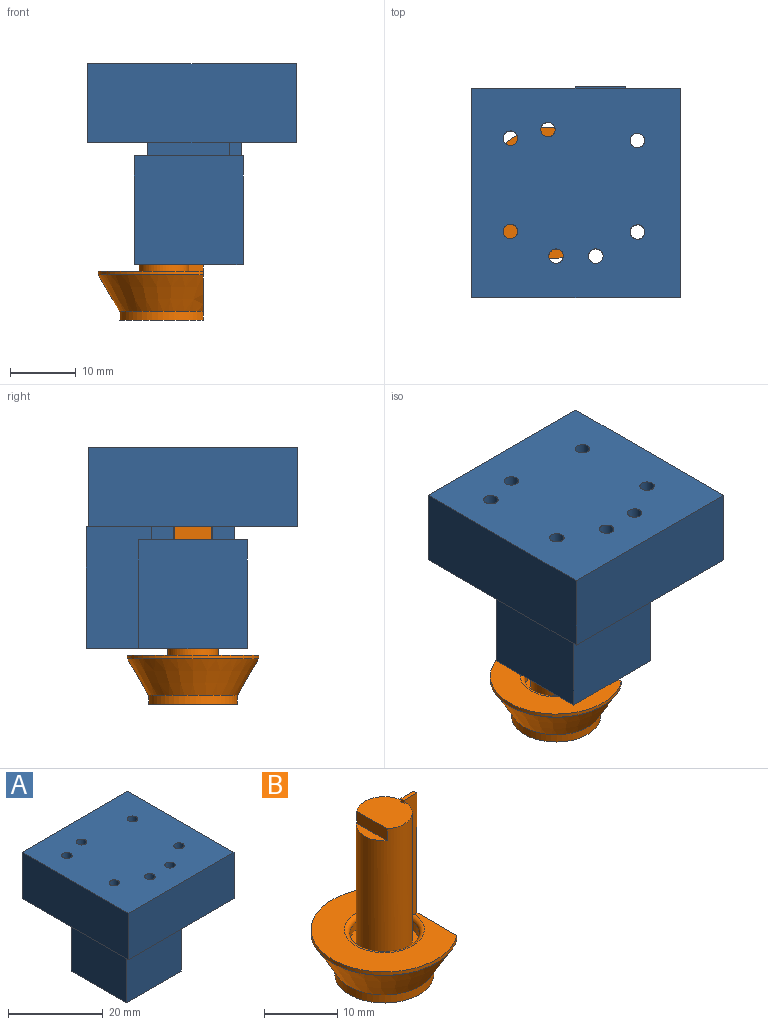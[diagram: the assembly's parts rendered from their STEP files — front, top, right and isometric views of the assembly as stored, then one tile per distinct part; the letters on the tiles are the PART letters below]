
ASSEMBLY  parts=2 mates=1
PART A: 31 faces, bbox 31.7x32.1x30.5 mm
  f0: plane 7.7x0.34mm, normal (0,0,1), area 2.6mm2, adj f10,f16,f17,f18
  f1: plane 16.51x0.16mm, normal (0,1,0), area 2.6mm2, adj f6,f7,f8,f16
  f2: plane 16.51x8.65mm, normal (0,1,0), area 142.8mm2, adj f3,f7,f8,f10
  f3: plane 16.51x16.51mm, normal (-1,0,0), area 272.6mm2, adj f2,f4,f7,f8
  f4: plane 16.51x16.51mm, normal (0,-1,0), area 272.6mm2, adj f3,f6,f7,f8
  f5: cylinder r=3.81mm len=18.51mm, axis (0,0,-1), area 430.1mm2, adj f7,f8,f12,f13,f30
  f6: plane 16.51x16.51mm, normal (1,0,0), area 272.6mm2, adj f1,f4,f7,f8
  f7: plane 16.51x16.51mm, normal (0,0,1), area 99.1mm2, adj f1,f2,f3,f4,f5,f6,f9,f10
  f8: plane 24.46x16.51mm, normal (0,0,-1), area 288.2mm2, adj f1,f2,f3,f4,f5,f6,f10,f16
  f9: plane 2x1.84mm, normal (0,-1,0), area 3.7mm2, adj f7,f15,f16,f30
  f10: plane 18.51x9.95mm, normal (-1,0,0), area 151.2mm2, adj f0,f2,f7,f8,f11,f17,f30
  f11: plane 6.65x2mm, normal (0,1,0), area 13.3mm2, adj f7,f10,f12,f30
  f12: plane 3.38x2mm, normal (-1,0,0), area 6.7mm2, adj f5,f7,f11,f30
  f13: plane 3.39x2mm, normal (-1,0,0), area 6.8mm2, adj f5,f7,f14,f30
  f14: plane 12.51x2mm, normal (0,-1,0), area 25mm2, adj f7,f13,f15,f30
  f15: plane 14.51x2mm, normal (1,0,0), area 29mm2, adj f7,f9,f14,f30
  f16: plane 18.51x7.95mm, normal (1,0,0), area 147.2mm2, adj f0,f1,f8,f9,f17,f30
  f17: plane 18.51x7.7mm, normal (0,1,0), area 142.5mm2, adj f0,f8,f10,f16
  f18: plane 31.69x12mm, normal (0,1,0), area 380.3mm2, adj f0,f19,f27,f29,f30
  f19: plane 31.76x12mm, normal (-1,0,0), area 381.1mm2, adj f18,f20,f29,f30
  f20: plane 31.69x12mm, normal (0,-1,0), area 380.3mm2, adj f19,f27,f29,f30
  f21: cylinder r=1.1mm len=12mm, axis (0,0,-1), area 82.9mm2, adj f29,f30
  f22: cylinder r=1.1mm len=12mm, axis (0,0,-1), area 82.9mm2, adj f29,f30
  f23: cylinder r=1.1mm len=12mm, axis (0,0,-1), area 82.9mm2, adj f29,f30
  f24: cylinder r=1.1mm len=12mm, axis (0,0,-1), area 82.9mm2, adj f29,f30
  f25: cylinder r=1.1mm len=12mm, axis (0,0,-1), area 82.9mm2, adj f29,f30
  f26: cylinder r=1.1mm len=12mm, axis (0,0,-1), area 82.9mm2, adj f29,f30
  f27: plane 31.76x12mm, normal (1,0,0), area 381.1mm2, adj f18,f20,f29,f30
  f28: cylinder r=1.1mm len=12mm, axis (0,0,-1), area 82.9mm2, adj f29,f30
  f29: plane 31.76x31.69mm, normal (0,0,1), area 979.8mm2, adj f18,f19,f20,f21,f22,f23,f24,f25
  f30: plane 31.76x31.69mm, normal (0,0,-1), area 793.3mm2, adj f5,f9,f10,f11,f12,f13,f14,f15
PART B: 19 faces, bbox 18.8x20x27.5 mm
  f0: plane 20x16mm, normal (0,0,1), area 175.8mm2, adj f1,f9,f13,f15,f17
  f1: cylinder r=10mm len=20mm, axis (0,0,1), area 26.6mm2, adj f0,f2,f13
  f2: plane 20x16mm, normal (0,0,-1), area 2.2mm2, adj f1,f4,f13
  f3: cylinder r=6.75mm len=13.5mm, axis (0,0,-1), area 48.5mm2, adj f4,f12,f13
  f4: cone r=9.95mm half-angle=30deg, axis (0,0,1), area 254.4mm2, adj f2,f3,f13
  f5: plane 7.62x6.2mm, normal (0,0,1), area 39.6mm2, adj f6,f10,f15,f16,f17
  f6: cylinder r=3.81mm len=21.51mm, axis (0,0,1), area 489.7mm2, adj f5,f8,f10,f11,f14,f15,f17
  f7: cylinder r=4.75mm len=9.5mm, axis (0,0,1), area 38.8mm2, adj f8,f9
  f8: plane 9.5x9.5mm, normal (0,0,1), area 25.3mm2, adj f6,f7
  f9: torus R=5.45mm, axis (0,0,1), area 34.6mm2, adj f0,f7,f14
  f10: plane 5.92x2mm, normal (-1,0,0), area 11.8mm2, adj f5,f6,f11
  f11: plane 5.92x1.41mm, normal (0,0,1), area 5.8mm2, adj f6,f10
  f12: plane 13.5x12.75mm, normal (0,0,-1), area 140mm2, adj f3,f13
  f13: plane 27.49x16mm, normal (1,0,0), area 93.3mm2, adj f0,f1,f2,f3,f4,f12,f15,f17
  f14: plane 1.65x0.6mm, normal (0,0,-1), area 1mm2, adj f6,f9,f15,f17
  f15: plane 20x2.5mm, normal (0,1,0), area 44.2mm2, adj f0,f5,f6,f13,f14,f16,f18
  f16: plane 0.6x0.49mm, normal (-1,0,0), area 0.3mm2, adj f5,f15,f17,f18
  f17: plane 20x2.5mm, normal (0,-1,0), area 44.2mm2, adj f0,f5,f6,f13,f14,f16,f18
  f18: plane 2.5x0.6mm, normal (0,0,1), area 1.5mm2, adj f13,f15,f16,f17
PLACE A t=(-4.66,6.84,0.82)mm
PLACE B t=(-4.66,6.84,-7.65)mm
MATE slider A.f5 <-> B.f6  axis (0,0,-1) through (-4.66,6.84,19.33)mm
